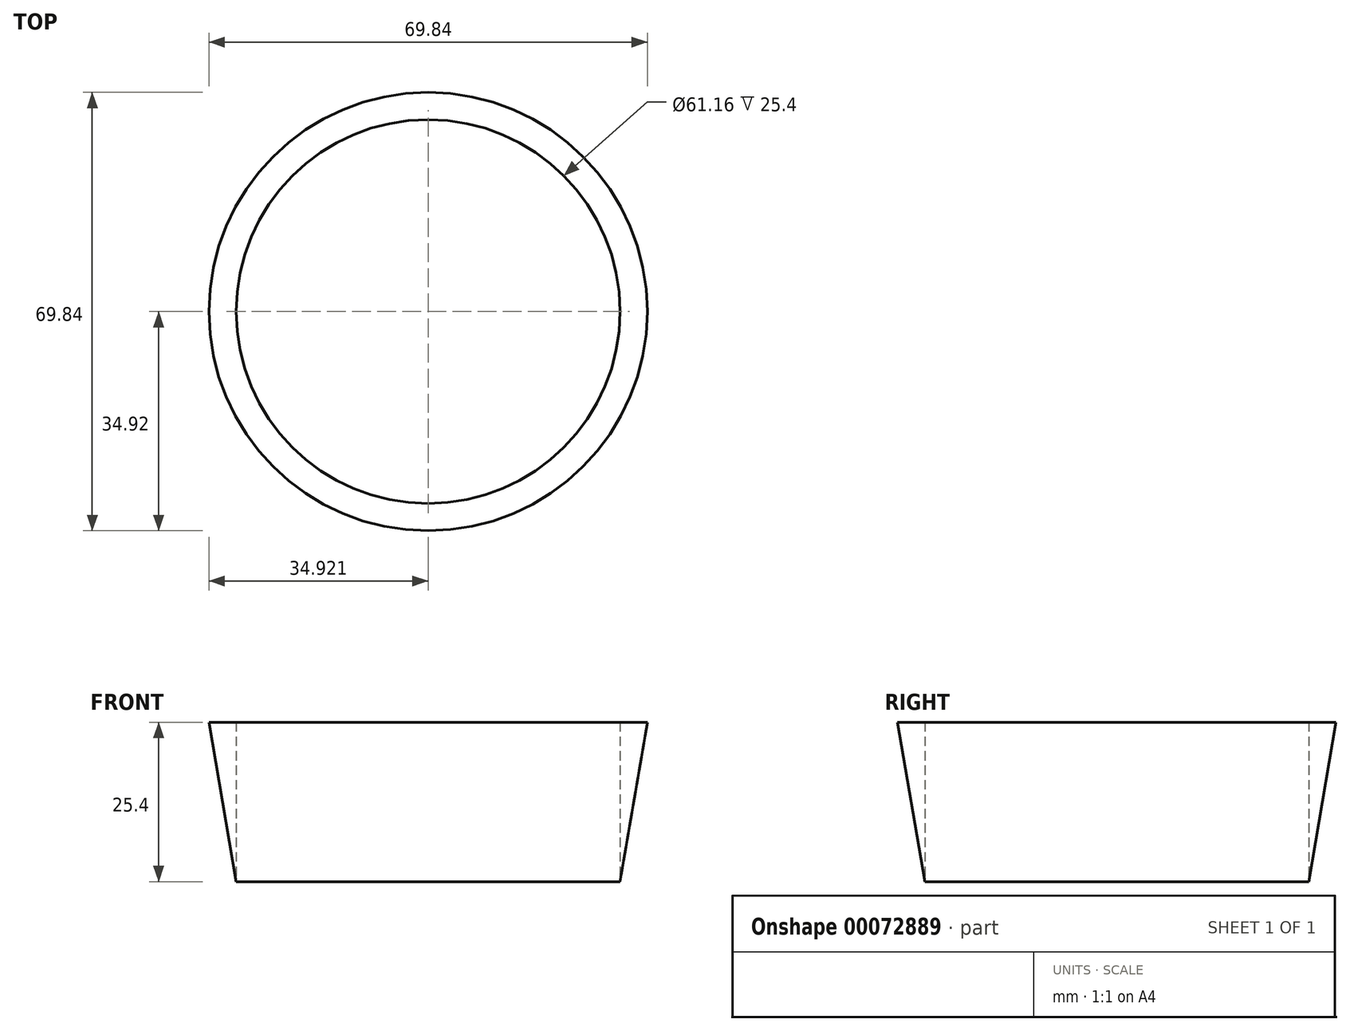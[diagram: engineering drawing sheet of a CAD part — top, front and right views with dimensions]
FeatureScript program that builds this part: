
annotation { "Feature Type Name" : "Feature", "Feature Type Description" : "" }
export const myFeature = defineFeature(function(context is Context, id is Id, definition is map)
    precondition{}
    {
        {
            var Q0;
            Q0=qCreatedBy(makeId("Top.planeOp"),FACE);
            var sketch = newSketch(context, id + "F0", { "sketchPlane" : qUnion([Q0])});
            skCircle(sketch, "E0", {"center": v(-103.97, 0) * mm, "radius": 30.58 * mm});
            skSolve(sketch);
        }
        {
            var Q0;
            Q0=makeQuery(id+"F0.imprint","IMPRINT",FACE,{"disambiguationData":[TD([[makeQuery(id+"F0.imprint","IMPRINT",EDGE,{"derivedFrom":sQuery(id+"F0.wireOp",EDGE,"E0")}),1.0]])]});
            extrude(context, id + "F1", {"entities" : qUnion([Q0]), "depth" : 25.4 * mm, "hasDraft" : true, "draftAngle" : 9.7 * degree});
        }
        {
            var Q0;
            Q0=sQuery(id+"F0.wireOp",VERTEX,"E0.center");
            var Q1;
            Q1=makeQuery(id+"F1.opExtrude","SWEPT_BODY",BODY,{"disambiguationData":[OSD([sQuery(id+"F0.wireOp",EDGE,"E0")])]});
            hole(context, id + "F2", {"style" : HoleStyle.SIMPLE, "holeDiameter" : 6.35 * mm, "endStyle" : HoleEndStyle.THROUGH, "locations" : qUnion([Q0]), "scope" : qUnion([Q1])});
        }
        {
            var Q0;
            Q0 = qSketchRegion(id + "F0", true);
            extrude(context, id + "F3", {"entities" : qUnion([Q0]), "operationType" : NewBodyOperationType.REMOVE, "depth" : 25.4 * mm});
        }
    });
